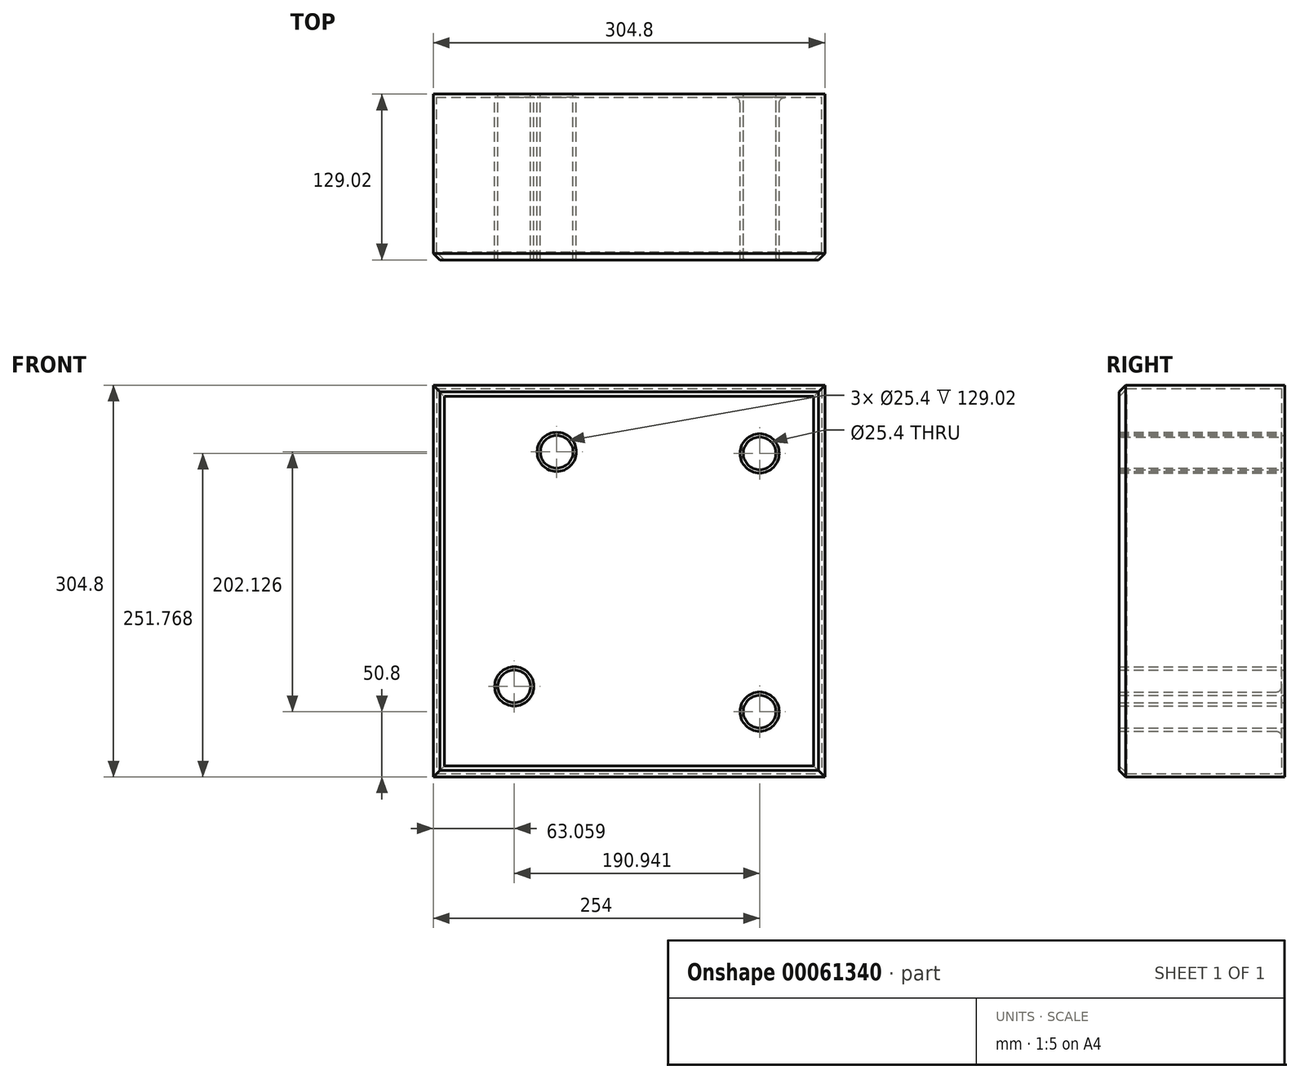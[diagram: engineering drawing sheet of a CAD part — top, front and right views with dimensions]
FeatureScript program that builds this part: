
annotation { "Feature Type Name" : "Feature", "Feature Type Description" : "" }
export const myFeature = defineFeature(function(context is Context, id is Id, definition is map)
    precondition{}
    {
        {
            var Q0;
            Q0=qCreatedBy(makeId("Front.planeOp"),FACE);
            var sketch = newSketch(context, id + "F0", { "sketchPlane" : qUnion([Q0])});
            skLineSegment(sketch, "E0.rect.bottom", {"start": v(-152.4, 152.4) * mm, "end": v(152.4, 152.4) * mm});
            skLineSegment(sketch, "E0.rect.top", {"start": v(-152.4, -152.4) * mm, "end": v(152.4, -152.4) * mm});
            skLineSegment(sketch, "E0.rect.left", {"start": v(-152.4, 152.4) * mm, "end": v(-152.4, -152.4) * mm});
            skLineSegment(sketch, "E0.rect.right", {"start": v(152.4, 152.4) * mm, "end": v(152.4, -152.4) * mm});
            skPoint(sketch, "E0.rect.middle", {"position": v(0, 0) * mm});
            skCircle(sketch, "E1", {"center": v(-56.32, 100.53) * mm, "radius": 12.7 * mm});
            skCircle(sketch, "E2", {"center": v(101.6, 99.37) * mm, "radius": 12.7 * mm});
            skCircle(sketch, "E3", {"center": v(-89.34, -81.99) * mm, "radius": 12.7 * mm});
            skCircle(sketch, "E4", {"center": v(101.6, -101.6) * mm, "radius": 12.7 * mm});
            skSolve(sketch);
        }
        {
            var Q0;
            Q0=makeQuery(id+"F0.imprint","IMPRINT",FACE,{"disambiguationData":[TD([[makeQuery(id+"F0.imprint","IMPRINT",EDGE,{"derivedFrom":sQuery(id+"F0.wireOp",EDGE,"E0.rect.bottom")}),-1.0]])]});
            extrude(context, id + "F1", {"entities" : qUnion([Q0]), "depth" : 129.02 * mm});
        }
        {
            var Q0;
            Q0=makeQuery(id+"F1.opExtrude","CAP_EDGE",EDGE,{"disambiguationData":[OSD([sQuery(id+"F0.wireOp",EDGE,"E0.rect.left")])],"isStart":false});
            var Q1;
            Q1=makeQuery(id+"F1.opExtrude","CAP_EDGE",EDGE,{"disambiguationData":[OSD([sQuery(id+"F0.wireOp",EDGE,"E0.rect.top")])],"isStart":false});
            var Q2;
            Q2=makeQuery(id+"F1.opExtrude","CAP_EDGE",EDGE,{"disambiguationData":[OSD([sQuery(id+"F0.wireOp",EDGE,"E0.rect.right")])],"isStart":false});
            var Q3;
            Q3=makeQuery(id+"F1.opExtrude","CAP_EDGE",EDGE,{"disambiguationData":[OSD([sQuery(id+"F0.wireOp",EDGE,"E0.rect.bottom")])],"isStart":false});
            chamfer(context, id + "F2", {"entities" : qUnion([Q0, Q1, Q2, Q3]), "width" : 5.08 * mm, "tangentPropagation" : true});
        }
        {
            var Q0;
            Q0=makeQuery(id+"F1.opExtrude","CAP_FACE",FACE,{"disambiguationData":[OSD([sQuery(id+"F0.wireOp",EDGE,"E0.rect.bottom"),sQuery(id+"F0.wireOp",EDGE,"E0.rect.top"),sQuery(id+"F0.wireOp",EDGE,"E0.rect.left"),sQuery(id+"F0.wireOp",EDGE,"E0.rect.right"),sQuery(id+"F0.wireOp",EDGE,"E1"),sQuery(id+"F0.wireOp",EDGE,"E2"),sQuery(id+"F0.wireOp",EDGE,"E3"),sQuery(id+"F0.wireOp",EDGE,"E4")])],"isStart":false});
            shell(context, id + "F3", {"entities" : qUnion([Q0]), "thickness" : 2.54 * mm});
        }
        {
            var Q0;
            {var subQ0=sQuery(id+"F0.wireOp",EDGE,"E4");Q0=makeQuery(id+"F3.opShell","OFFSET_EDGE",EDGE,{"disambiguationData":[OSD([subQ0]),TDD([makeQuery(id+"F1.opExtrude","CAP_EDGE",EDGE,{"disambiguationData":[OSD([subQ0])],"isStart":true})])]});}
            fillet(context, id + "F4", {"entities" : qUnion([Q0]), "radius" : 5.08 * mm, "tangentPropagation" : true, "rho" : 0.5, "crossSection" : FilletCrossSection.CONIC, "allowEdgeOverflow" : false});
        }
        {
            var Q0;
            Q0=makeQuery(id+"F1.opExtrude","CAP_EDGE",EDGE,{"disambiguationData":[OSD([sQuery(id+"F0.wireOp",EDGE,"E2")])],"isStart":false});
            fillet(context, id + "F5", {"entities" : qUnion([Q0]), "radius" : 1.55 * mm, "tangentPropagation" : true, "allowEdgeOverflow" : false});
        }
    });
